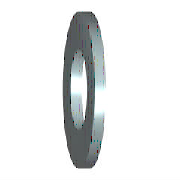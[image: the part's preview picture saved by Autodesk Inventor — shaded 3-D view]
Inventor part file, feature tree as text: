
AUTODESK INVENTOR PART (.ipt)
format: ipt  version: 2024.3 (Build 283343000, 343)  size: 103,424 bytes
history: native  units: mm (DEFAULTED — no unit token found)
features: other x1, plane x1
ambient origin geometry x7: Origin, YZ Plane, XY Plane, X Axis, Y Axis, Z Axis, Center Point
bodies: Solid1 (feature_tree), Body (feature_tree)
feature tree (2):
  other  "Work Axis1"
  plane  "Work Plane1"
